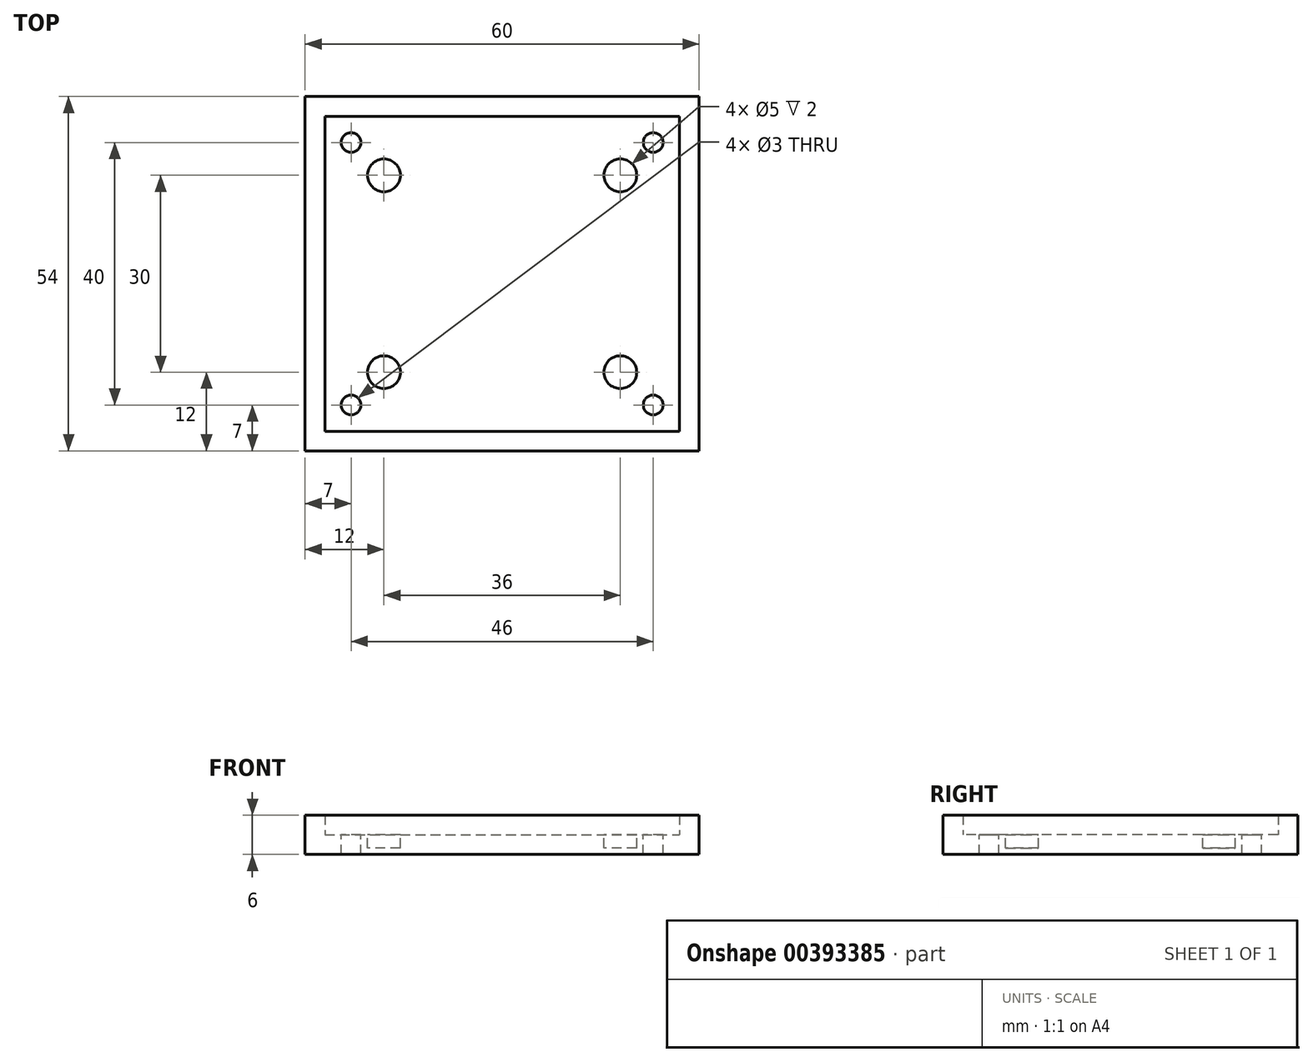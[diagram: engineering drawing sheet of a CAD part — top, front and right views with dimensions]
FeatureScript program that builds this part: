
annotation { "Feature Type Name" : "Feature", "Feature Type Description" : "" }
export const myFeature = defineFeature(function(context is Context, id is Id, definition is map)
    precondition{}
    {
        {
            var Q0;
            Q0=qCreatedBy(makeId("Top.planeOp"),FACE);
            var sketch = newSketch(context, id + "F0", { "sketchPlane" : qUnion([Q0])});
            skLineSegment(sketch, "E0.bottom", {"start": v(-27, 24) * mm, "end": v(27, 24) * mm});
            skLineSegment(sketch, "E0.top", {"start": v(-27, -24) * mm, "end": v(27, -24) * mm});
            skLineSegment(sketch, "E0.left", {"start": v(-27, 24) * mm, "end": v(-27, -24) * mm});
            skLineSegment(sketch, "E0.right", {"start": v(27, 24) * mm, "end": v(27, -24) * mm});
            skPoint(sketch, "E0.middle", {"position": v(0, 0) * mm});
            skLineSegment(sketch, "E1.bottom", {"start": v(-30, 27) * mm, "end": v(30, 27) * mm});
            skLineSegment(sketch, "E1.top", {"start": v(-30, -27) * mm, "end": v(30, -27) * mm});
            skLineSegment(sketch, "E1.left", {"start": v(-30, 27) * mm, "end": v(-30, -27) * mm});
            skLineSegment(sketch, "E1.right", {"start": v(30, 27) * mm, "end": v(30, -27) * mm});
            skSolve(sketch);
        }
        {
            var Q0;
            Q0=makeQuery(id+"F0.imprint","IMPRINT",FACE,{"disambiguationData":[TD([[makeQuery(id+"F0.imprint","IMPRINT",EDGE,{"derivedFrom":sQuery(id+"F0.wireOp",EDGE,"E0.bottom")}),1.0]])]});
            var Q1;
            Q1=makeQuery(id+"F0.imprint","IMPRINT",FACE,{"disambiguationData":[TD([[makeQuery(id+"F0.imprint","IMPRINT",EDGE,{"derivedFrom":sQuery(id+"F0.wireOp",EDGE,"E0.bottom")}),-1.0]])]});
            extrude(context, id + "F1", {"entities" : qUnion([Q0, Q1]), "oppositeDirection" : true, "depth" : 3 * mm});
        }
        {
            var Q0;
            Q0 = qSketchRegion(id + "F0", true);
            extrude(context, id + "F2", {"entities" : qUnion([Q0]), "operationType" : NewBodyOperationType.ADD, "depth" : 3 * mm});
        }
        {
            var Q0;
            Q0=makeQuery(id+"F1.opExtrude","CAP_FACE",FACE,{"disambiguationData":[OSD([sQuery(id+"F0.wireOp",EDGE,"E1.bottom"),sQuery(id+"F0.wireOp",EDGE,"E1.top"),sQuery(id+"F0.wireOp",EDGE,"E1.left"),sQuery(id+"F0.wireOp",EDGE,"E1.right")])],"isStart":true});
            var sketch = newSketch(context, id + "F3", { "sketchPlane" : qUnion([Q0])});
            skCircle(sketch, "E2", {"center": v(-18, 15) * mm, "radius": 2.5 * mm});
            skCircle(sketch, "E3.MirrorC", {"center": v(18, 15) * mm, "radius": 2.5 * mm});
            skCircle(sketch, "E4.MirrorC", {"center": v(18, -15) * mm, "radius": 2.5 * mm});
            skCircle(sketch, "E5.MirrorC", {"center": v(-18, -15) * mm, "radius": 2.5 * mm});
            skSolve(sketch);
        }
        {
            var Q0;
            Q0 = qSketchRegion(id + "F3", true);
            extrude(context, id + "F4", {"entities" : qUnion([Q0]), "operationType" : NewBodyOperationType.REMOVE, "oppositeDirection" : true, "depth" : 2 * mm});
        }
        {
            var Q0;
            Q0=makeQuery(id+"F1.opExtrude","CAP_FACE",FACE,{"disambiguationData":[OSD([sQuery(id+"F0.wireOp",EDGE,"E1.bottom"),sQuery(id+"F0.wireOp",EDGE,"E1.top"),sQuery(id+"F0.wireOp",EDGE,"E1.left"),sQuery(id+"F0.wireOp",EDGE,"E1.right")])],"isStart":true});
            var sketch = newSketch(context, id + "F5", { "sketchPlane" : qUnion([Q0])});
            skCircle(sketch, "E6", {"center": v(-23, 20) * mm, "radius": 1.5 * mm});
            skCircle(sketch, "E7.MirrorC", {"center": v(23, 20) * mm, "radius": 1.5 * mm});
            skCircle(sketch, "E8.MirrorC", {"center": v(-23, -20) * mm, "radius": 1.5 * mm});
            skCircle(sketch, "E9.MirrorC", {"center": v(23, -20) * mm, "radius": 1.5 * mm});
            skSolve(sketch);
        }
        {
            var Q0;
            Q0 = qSketchRegion(id + "F5", true);
            extrude(context, id + "F6", {"entities" : qUnion([Q0]), "operationType" : NewBodyOperationType.REMOVE, "endBound" : BoundingType.UP_TO_NEXT, "oppositeDirection" : true, "depth" : 25 * mm});
        }
    });
